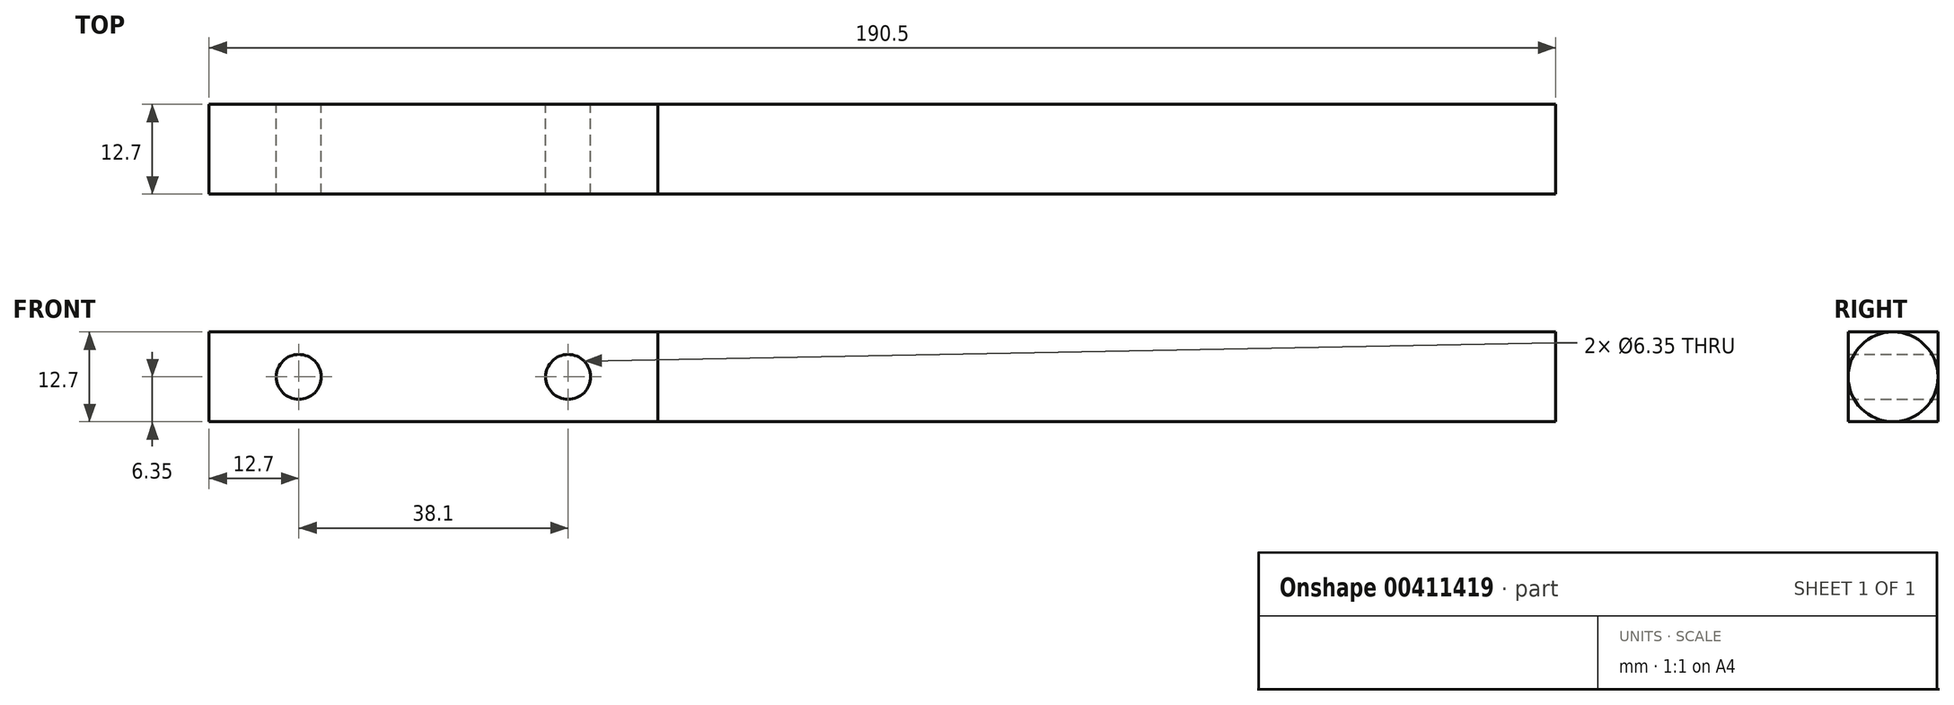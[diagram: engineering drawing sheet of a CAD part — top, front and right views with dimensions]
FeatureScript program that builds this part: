
annotation { "Feature Type Name" : "Feature", "Feature Type Description" : "" }
export const myFeature = defineFeature(function(context is Context, id is Id, definition is map)
    precondition{}
    {
        {
            var Q0;
            Q0=qCreatedBy(makeId("Front.planeOp"),FACE);
            var sketch = newSketch(context, id + "F0", { "sketchPlane" : qUnion([Q0])});
            skLineSegment(sketch, "E0.bottom", {"start": v(0, -6.35) * mm, "end": v(63.5, -6.35) * mm});
            skLineSegment(sketch, "E0.top", {"start": v(0, 6.35) * mm, "end": v(63.5, 6.35) * mm});
            skLineSegment(sketch, "E0.left", {"start": v(0, -6.35) * mm, "end": v(0, 6.35) * mm});
            skLineSegment(sketch, "E0.right", {"start": v(63.5, -6.35) * mm, "end": v(63.5, 6.35) * mm});
            skCircle(sketch, "E1", {"center": v(12.7, 0) * mm, "radius": 3.18 * mm});
            skCircle(sketch, "E2", {"center": v(50.8, 0) * mm, "radius": 3.18 * mm});
            skSolve(sketch);
        }
        {
            var Q0;
            Q0 = qSketchRegion(id + "F0", true);
            extrude(context, id + "F1", {"entities" : qUnion([Q0]), "endBound" : BoundingType.SYMMETRIC, "depth" : 12.7 * mm});
        }
        {
            var Q0;
            Q0=makeQuery(id+"F1.opExtrude","SWEPT_FACE",FACE,{"disambiguationData":[OSD([sQuery(id+"F0.wireOp",EDGE,"E0.right")])]});
            var sketch = newSketch(context, id + "F2", { "sketchPlane" : qUnion([Q0])});
            skCircle(sketch, "E3", {"center": v(0, 0) * mm, "radius": 6.35 * mm});
            skSolve(sketch);
        }
        {
            var Q0;
            Q0 = qSketchRegion(id + "F2", true);
            extrude(context, id + "F3", {"entities" : qUnion([Q0]), "operationType" : NewBodyOperationType.ADD, "depth" : 127 * mm});
        }
    });
